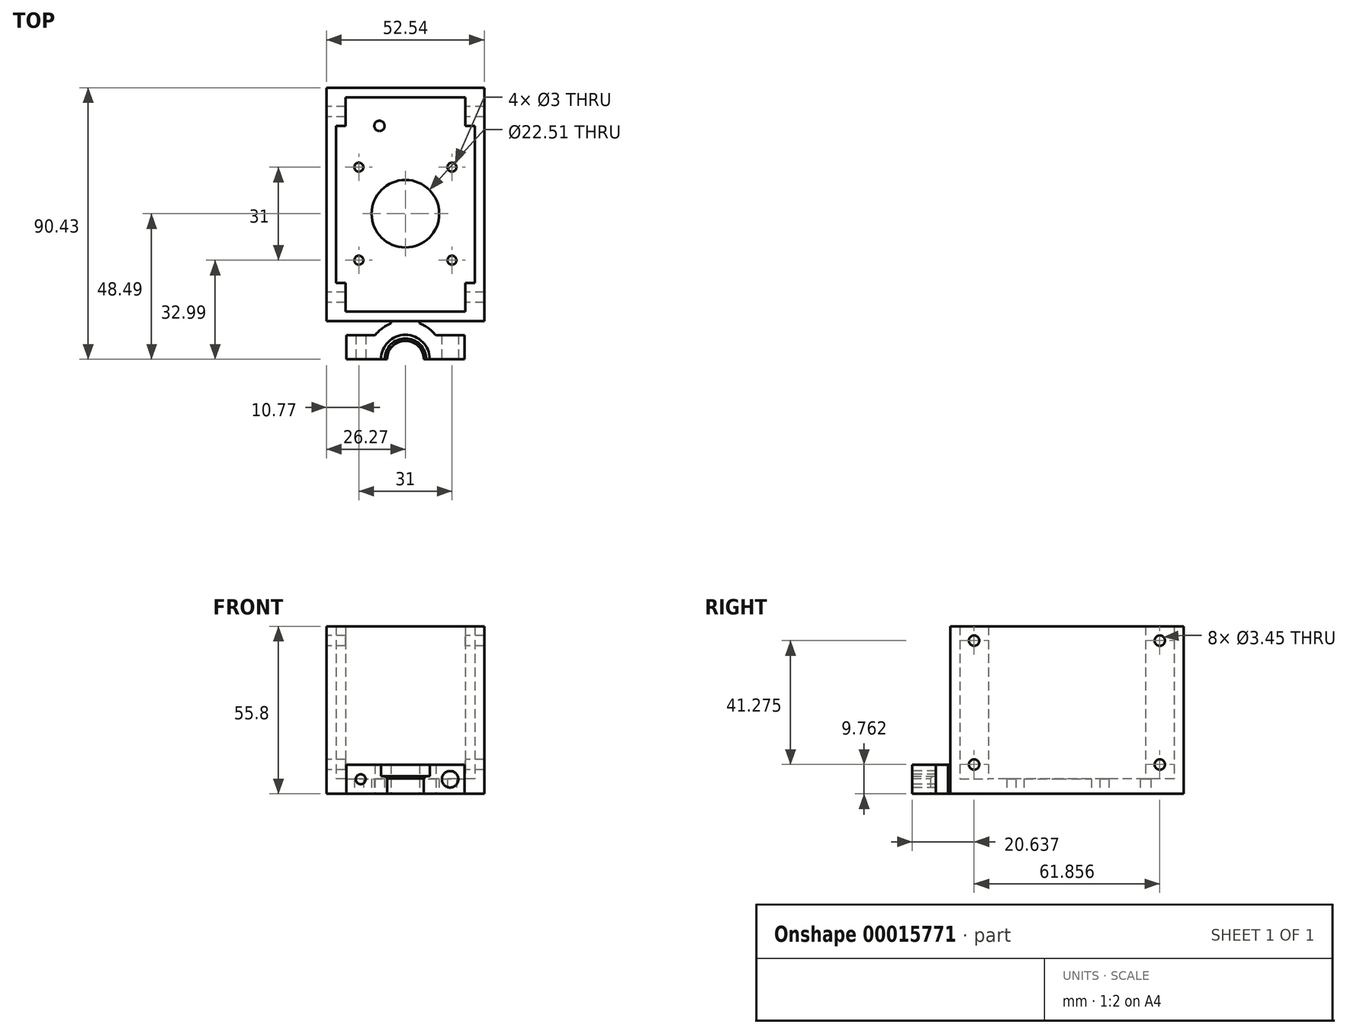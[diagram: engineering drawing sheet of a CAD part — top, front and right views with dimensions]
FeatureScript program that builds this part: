
annotation { "Feature Type Name" : "Feature", "Feature Type Description" : "" }
export const myFeature = defineFeature(function(context is Context, id is Id, definition is map)
    precondition{}
    {
        {
            var Q0;
            Q0=qCreatedBy(makeId("Top.planeOp"),FACE);
            var sketch = newSketch(context, id + "F0", { "sketchPlane" : qUnion([Q0])});
            skPoint(sketch, "E0.middle", {"position": v(0, 0) * mm});
            skLineSegment(sketch, "E1.bottom", {"start": v(-15.5, 15.5) * mm, "end": v(15.5, 15.5) * mm, "construction": true});
            skLineSegment(sketch, "E1.top", {"start": v(-15.5, -15.5) * mm, "end": v(15.5, -15.5) * mm, "construction": true});
            skLineSegment(sketch, "E1.left", {"start": v(-15.5, 15.5) * mm, "end": v(-15.5, -15.5) * mm, "construction": true});
            skLineSegment(sketch, "E1.right", {"start": v(15.5, 15.5) * mm, "end": v(15.5, -15.5) * mm, "construction": true});
            skCircle(sketch, "E2", {"center": v(0, 0) * mm, "radius": 11.25 * mm});
            skCircle(sketch, "E3", {"center": v(15.5, -15.5) * mm, "radius": 1.5 * mm});
            skCircle(sketch, "E4", {"center": v(15.5, 15.5) * mm, "radius": 1.5 * mm});
            skCircle(sketch, "E5", {"center": v(-15.5, 15.5) * mm, "radius": 1.5 * mm});
            skCircle(sketch, "E6", {"center": v(-15.5, -15.5) * mm, "radius": 1.5 * mm});
            skCircle(sketch, "E7", {"center": v(0, 0) * mm, "radius": 6.35 * mm, "construction": true});
            skCircle(sketch, "E8", {"center": v(-8.63, 29.24) * mm, "radius": 11.11 * mm, "construction": true});
            skLineSegment(sketch, "E9", {"start": v(-6.02, 2.01) * mm, "end": v(1.9, 25.72) * mm});
            skCircle(sketch, "E10", {"center": v(-8.63, 29.24) * mm, "radius": 1.73 * mm});
            skLineSegment(sketch, "E11", {"start": v(-8.63, 29.24) * mm, "end": v(-8.63, 0) * mm, "construction": true});
            skLineSegment(sketch, "E12", {"start": v(-8.63, 0) * mm, "end": v(0, 0) * mm, "construction": true});
            skCircle(sketch, "E13", {"center": v(-15.5, 15.5) * mm, "radius": 4.25 * mm, "construction": true});
            skLineSegment(sketch, "E14", {"start": v(-19.75, 29.24) * mm, "end": v(-19.75, 15.5) * mm, "construction": true});
            skLineSegment(sketch, "E15", {"start": v(-8.63, 29.24) * mm, "end": v(-8.63, 41.94) * mm, "construction": true});
            skLineSegment(sketch, "E16", {"start": v(0, 0) * mm, "end": v(0, -35.8) * mm, "construction": true});
            skLineSegment(sketch, "E17.bottom", {"start": v(26.27, -35.8) * mm, "end": v(-26.27, -35.8) * mm});
            skLineSegment(sketch, "E17.top", {"start": v(26.27, 41.94) * mm, "end": v(-26.27, 41.94) * mm});
            skLineSegment(sketch, "E17.left", {"start": v(26.27, -35.8) * mm, "end": v(26.27, 41.94) * mm});
            skLineSegment(sketch, "E17.right", {"start": v(-26.27, -35.8) * mm, "end": v(-26.27, 41.94) * mm});
            skSolve(sketch);
        }
        {
            var Q0;
            Q0=qSketchRegion(id+"F0",true);
            extrude(context, id + "F1", {"entities" : qUnion([Q0]), "depth" : 5 * mm});
        }
        {
            var Q0;
            Q0=makeQuery(id+"F1.opExtrude","CAP_FACE",FACE,{"disambiguationData":[OSD([sQuery(id+"F0.wireOp",EDGE,"E0.bottom"),sQuery(id+"F0.wireOp",EDGE,"E0.top"),sQuery(id+"F0.wireOp",EDGE,"E0.left"),sQuery(id+"F0.wireOp",EDGE,"E0.right"),sQuery(id+"F0.wireOp",EDGE,"E2"),sQuery(id+"F0.wireOp",EDGE,"E3"),sQuery(id+"F0.wireOp",EDGE,"E4"),sQuery(id+"F0.wireOp",EDGE,"E5"),sQuery(id+"F0.wireOp",EDGE,"E6")])],"isStart":false});
            var sketch = newSketch(context, id + "F2", { "sketchPlane" : qUnion([Q0])});
            skLineSegment(sketch, "E18.bottom", {"start": v(-26.27, 41.94) * mm, "end": v(26.27, 41.94) * mm});
            skLineSegment(sketch, "E18.top", {"start": v(-26.27, -35.8) * mm, "end": v(26.27, -35.8) * mm});
            skLineSegment(sketch, "E18.left", {"start": v(-26.27, 41.94) * mm, "end": v(-26.27, -35.8) * mm});
            skLineSegment(sketch, "E18.right", {"start": v(26.27, 41.94) * mm, "end": v(26.27, -35.8) * mm});
            skLineSegment(sketch, "E19", {"start": v(-19.92, 38.77) * mm, "end": v(-19.92, 41.94) * mm, "construction": true});
            skLineSegment(sketch, "E20", {"start": v(-19.92, 38.77) * mm, "end": v(-26.27, 38.77) * mm, "construction": true});
            skLineSegment(sketch, "E21", {"start": v(-19.92, 38.77) * mm, "end": v(19.92, 38.77) * mm});
            skLineSegment(sketch, "E22", {"start": v(-19.92, 38.77) * mm, "end": v(-19.92, 29.24) * mm});
            skLineSegment(sketch, "E23", {"start": v(-19.92, 29.24) * mm, "end": v(-23.1, 29.24) * mm});
            skLineSegment(sketch, "E24", {"start": v(-23.1, 29.24) * mm, "end": v(-23.1, -23.1) * mm});
            skLineSegment(sketch, "E25", {"start": v(19.92, 38.77) * mm, "end": v(19.92, 29.24) * mm});
            skLineSegment(sketch, "E26", {"start": v(19.92, 29.24) * mm, "end": v(23.1, 29.24) * mm});
            skLineSegment(sketch, "E27", {"start": v(23.1, 29.24) * mm, "end": v(23.1, -23.1) * mm});
            skLineSegment(sketch, "E28", {"start": v(23.1, -23.1) * mm, "end": v(19.92, -23.1) * mm});
            skLineSegment(sketch, "E29", {"start": v(19.92, -23.1) * mm, "end": v(19.92, -32.62) * mm});
            skLineSegment(sketch, "E30", {"start": v(19.92, -32.62) * mm, "end": v(-19.92, -32.62) * mm});
            skLineSegment(sketch, "E31", {"start": v(19.92, -32.62) * mm, "end": v(26.27, -32.62) * mm, "construction": true});
            skLineSegment(sketch, "E32", {"start": v(19.92, -32.62) * mm, "end": v(19.92, -35.8) * mm, "construction": true});
            skLineSegment(sketch, "E33", {"start": v(-19.92, -32.62) * mm, "end": v(-19.92, -23.1) * mm});
            skLineSegment(sketch, "E34", {"start": v(-19.92, -23.1) * mm, "end": v(-23.1, -23.1) * mm});
            skSolve(sketch);
        }
        {
            var Q0;
            Q0=qSketchRegion(id+"F2",true);
            extrude(context, id + "F3", {"entities" : qUnion([Q0]), "operationType" : NewBodyOperationType.ADD, "depth" : 50.8 * mm});
        }
        {
            var Q0;
            Q0=makeQuery(id+"F3.boolean.opBoolean","MERGE",FACE,{"derivedFrom":[makeQuery(id+"F1.opExtrude","SWEPT_FACE",FACE,{"disambiguationData":[OSD([sQuery(id+"F0.wireOp",EDGE,"E0.right")])]}),makeQuery(id+"F3.opExtrude","SWEPT_FACE",FACE,{"disambiguationData":[OSD([sQuery(id+"F2.wireOp",EDGE,"E18.left")])]})]});
            var sketch = newSketch(context, id + "F4", { "sketchPlane" : qUnion([Q0])});
            skLineSegment(sketch, "E35.bottom", {"start": v(-34, 51.04) * mm, "end": v(27.85, 51.04) * mm, "construction": true});
            skLineSegment(sketch, "E35.top", {"start": v(-34, 9.76) * mm, "end": v(27.85, 9.76) * mm, "construction": true});
            skLineSegment(sketch, "E35.left", {"start": v(-34, 51.04) * mm, "end": v(-34, 9.76) * mm, "construction": true});
            skLineSegment(sketch, "E35.right", {"start": v(27.85, 51.04) * mm, "end": v(27.85, 9.76) * mm, "construction": true});
            skCircle(sketch, "E36", {"center": v(-34, 51.04) * mm, "radius": 1.73 * mm});
            skCircle(sketch, "E37", {"center": v(27.85, 51.04) * mm, "radius": 1.73 * mm});
            skCircle(sketch, "E38", {"center": v(27.85, 9.76) * mm, "radius": 1.73 * mm});
            skCircle(sketch, "E39", {"center": v(-34, 9.76) * mm, "radius": 1.73 * mm});
            skLineSegment(sketch, "E40", {"start": v(27.85, 51.04) * mm, "end": v(27.85, 55.8) * mm, "construction": true});
            skLineSegment(sketch, "E41", {"start": v(-34, 51.04) * mm, "end": v(-34, 55.8) * mm, "construction": true});
            skLineSegment(sketch, "E42", {"start": v(-3.07, 9.76) * mm, "end": v(-3.07, 5) * mm, "construction": true});
            skSolve(sketch);
        }
        {
            var Q0;
            Q0=qSketchRegion(id+"F4",true);
            var Q1;
            Q1=makeQuery(id+"F3.boolean.opBoolean","MERGE",FACE,{"derivedFrom":[makeQuery(id+"F1.opExtrude","SWEPT_FACE",FACE,{"disambiguationData":[OSD([sQuery(id+"F0.wireOp",EDGE,"E0.left")])]}),makeQuery(id+"F3.opExtrude","SWEPT_FACE",FACE,{"disambiguationData":[OSD([sQuery(id+"F2.wireOp",EDGE,"E18.right")])]})]});
            extrude(context, id + "F5", {"entities" : qUnion([Q0]), "operationType" : NewBodyOperationType.REMOVE, "endBound" : BoundingType.UP_TO_SURFACE, "oppositeDirection" : true, "endBoundEntityFace" : qUnion([Q1]), "depth" : 25.4 * mm});
        }
        {
            var Q0;
            Q0=makeQuery(id+"F1.opExtrude","CAP_FACE",FACE,{"disambiguationData":[OSD([sQuery(id+"F0.wireOp",EDGE,"E2"),sQuery(id+"F0.wireOp",EDGE,"E3"),sQuery(id+"F0.wireOp",EDGE,"E4"),sQuery(id+"F0.wireOp",EDGE,"E5"),sQuery(id+"F0.wireOp",EDGE,"E6"),sQuery(id+"F0.wireOp",EDGE,"E10"),sQuery(id+"F0.wireOp",EDGE,"E17.bottom"),sQuery(id+"F0.wireOp",EDGE,"E17.top"),sQuery(id+"F0.wireOp",EDGE,"E17.left"),sQuery(id+"F0.wireOp",EDGE,"E17.right")])],"isStart":true});
            var sketch = newSketch(context, id + "F6", { "sketchPlane" : qUnion([Q0])});
            skLineSegment(sketch, "E43.bottom", {"start": v(-4.76, 35.8) * mm, "end": v(4.76, 35.8) * mm});
            skLineSegment(sketch, "E43.left", {"start": v(-4.76, 35.8) * mm, "end": v(-4.76, 36.54) * mm});
            skLineSegment(sketch, "E43.right", {"start": v(4.76, 35.8) * mm, "end": v(4.76, 36.54) * mm});
            skArc(sketch, "E44", {"start": v(-10.12, 40.55) * mm, "mid": v(-7.7, 38.2) * mm, "end": v(-4.76, 36.54) * mm});
            skArc(sketch, "E45", {"start": v(4.76, 36.54) * mm, "mid": v(7.7, 38.2) * mm, "end": v(10.12, 40.55) * mm});
            skLineSegment(sketch, "E46", {"start": v(0, 35.8) * mm, "end": v(0, 48.5) * mm, "construction": true});
            skLineSegment(sketch, "E47.bottom", {"start": v(-10.12, 40.55) * mm, "end": v(-19.65, 40.55) * mm});
            skLineSegment(sketch, "E47.top", {"start": v(-6.12, 48.5) * mm, "end": v(-19.65, 48.5) * mm});
            skLineSegment(sketch, "E47.right", {"start": v(-19.65, 40.55) * mm, "end": v(-19.65, 48.5) * mm});
            skLineSegment(sketch, "E48.bottom", {"start": v(10.12, 40.55) * mm, "end": v(19.65, 40.55) * mm});
            skLineSegment(sketch, "E48.top", {"start": v(6.12, 48.5) * mm, "end": v(19.65, 48.5) * mm});
            skLineSegment(sketch, "E48.right", {"start": v(19.65, 40.55) * mm, "end": v(19.65, 48.5) * mm});
            skLineSegment(sketch, "E49", {"start": v(-6.12, 48.5) * mm, "end": v(6.12, 48.5) * mm, "construction": true});
            skArc(sketch, "E50", {"start": v(-6.12, 48.5) * mm, "mid": v(0, 42.37) * mm, "end": v(6.12, 48.5) * mm});
            skSolve(sketch);
        }
        {
            var Q0;
            Q0 = qSketchRegion(id + "F6", true);
            extrude(context, id + "F7", {"entities" : qUnion([Q0]), "operationType" : NewBodyOperationType.ADD, "oppositeDirection" : true, "depth" : 9.68 * mm});
        }
        {
            var Q0;
            Q0=makeQuery(id+"F7.opExtrude","CAP_FACE",FACE,{"disambiguationData":[OSD([sQuery(id+"F6.wireOp",EDGE,"E43.bottom"),sQuery(id+"F6.wireOp",EDGE,"E43.left"),sQuery(id+"F6.wireOp",EDGE,"E43.right"),sQuery(id+"F6.wireOp",EDGE,"E44"),sQuery(id+"F6.wireOp",EDGE,"E45"),sQuery(id+"F6.wireOp",EDGE,"E47.bottom"),sQuery(id+"F6.wireOp",EDGE,"E47.top"),sQuery(id+"F6.wireOp",EDGE,"E47.right"),sQuery(id+"F6.wireOp",EDGE,"E48.bottom"),sQuery(id+"F6.wireOp",EDGE,"E48.top"),sQuery(id+"F6.wireOp",EDGE,"E48.right"),sQuery(id+"F6.wireOp",EDGE,"E50")])],"isStart":false});
            var sketch = newSketch(context, id + "F8", { "sketchPlane" : qUnion([Q0])});
            skArc(sketch, "E51", {"start": v(8.1, -48.5) * mm, "mid": v(0, -40.39) * mm, "end": v(-8.1, -48.5) * mm});
            skLineSegment(sketch, "E52", {"start": v(-8.1, -48.5) * mm, "end": v(8.1, -48.5) * mm});
            skSolve(sketch);
        }
        {
            var Q0;
            Q0 = qSketchRegion(id + "F8", true);
            extrude(context, id + "F9", {"entities" : qUnion([Q0]), "operationType" : NewBodyOperationType.REMOVE, "oppositeDirection" : true, "depth" : 3.8 * mm});
        }
        {
            var Q0;
            Q0=makeQuery(id+"F7.opExtrude","SWEPT_FACE",FACE,{"disambiguationData":[OSD([sQuery(id+"F6.wireOp",EDGE,"E47.top")])]});
            var sketch = newSketch(context, id + "F10", { "sketchPlane" : qUnion([Q0])});
            skLineSegment(sketch, "E53", {"start": v(-19.65, 4.84) * mm, "end": v(-14.89, 4.84) * mm, "construction": true});
            skLineSegment(sketch, "E54", {"start": v(-14.89, 4.84) * mm, "end": v(14.89, 4.84) * mm, "construction": true});
            skLineSegment(sketch, "E55", {"start": v(14.89, 4.84) * mm, "end": v(19.65, 4.84) * mm, "construction": true});
            skCircle(sketch, "E56", {"center": v(-14.89, 4.84) * mm, "radius": 1.65 * mm});
            skCircle(sketch, "E57", {"center": v(14.89, 4.84) * mm, "radius": 2.75 * mm});
            skSolve(sketch);
        }
        {
            var Q0;
            Q0 = qSketchRegion(id + "F10", true);
            var Q1;
            Q1=makeQuery(id+"F7.opExtrude","SWEPT_FACE",FACE,{"disambiguationData":[OSD([sQuery(id+"F6.wireOp",EDGE,"E47.bottom")])]});
            extrude(context, id + "F11", {"entities" : qUnion([Q0]), "operationType" : NewBodyOperationType.REMOVE, "endBound" : BoundingType.UP_TO_SURFACE, "oppositeDirection" : true, "endBoundEntityFace" : qUnion([Q1]), "depth" : 25.4 * mm});
        }
        {
            var Q0;
            Q0=makeQuery(id+"F9.boolean.opBoolean","INTERSECT",EDGE,{"derivedFrom":[makeQuery(id+"F7.opExtrude","SWEPT_FACE",FACE,{"disambiguationData":[OSD([sQuery(id+"F6.wireOp",EDGE,"E50")])]}),makeQuery(id+"F9.opExtrude","CAP_FACE",FACE,{"disambiguationData":[OSD([sQuery(id+"F8.wireOp",EDGE,"E51"),sQuery(id+"F8.wireOp",EDGE,"E52")])],"isStart":false})]});
            chamfer(context, id + "F12", {"entities" : qUnion([Q0]), "width" : 0.8 * mm, "tangentPropagation" : true});
        }
    });
